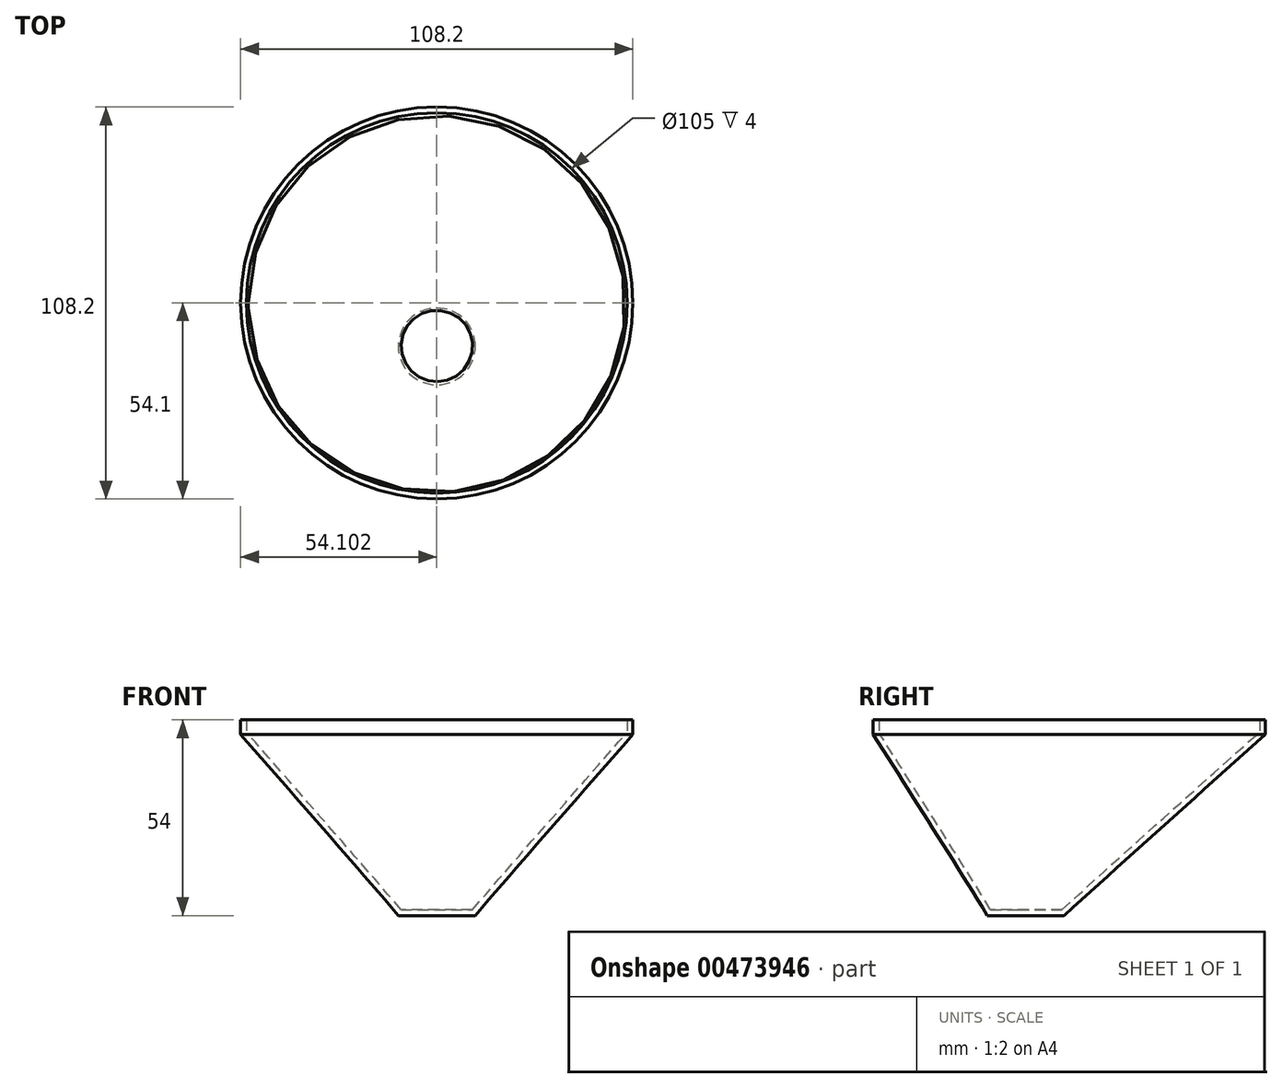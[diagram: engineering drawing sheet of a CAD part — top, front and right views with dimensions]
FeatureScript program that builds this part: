
annotation { "Feature Type Name" : "Feature", "Feature Type Description" : "" }
export const myFeature = defineFeature(function(context is Context, id is Id, definition is map)
    precondition{}
    {
        {
            var Q0;
            Q0=qCreatedBy(makeId("Top.planeOp"),FACE);
            var sketch = newSketch(context, id + "F0", { "sketchPlane" : qUnion([Q0])});
            skCircle(sketch, "E0", {"center": v(-6, 0) * mm, "radius": 52.5 * mm, "construction": true});
            skCircle(sketch, "E1.0", {"center": v(-6, 0) * mm, "radius": 54.1 * mm});
            skSolve(sketch);
        }
        {
            var Q0;
            Q0=qCreatedBy(makeId("Top.planeOp"),FACE);
            cPlane(context, id + "F1", {"entities" : qUnion([Q0]), "cplaneType" : CPlaneType.OFFSET, "offset" : 50 * mm, "oppositeDirection" : true, "width" : 150 * mm, "height" : 150 * mm});
        }
        {
            var Q0;
            Q0=qCreatedBy(id+"F1.planeOp",FACE);
            var sketch = newSketch(context, id + "F2", { "sketchPlane" : qUnion([Q0])});
            skPoint(sketch, "E2.0", {"position": v(-6, 0) * mm});
            skCircle(sketch, "E3", {"center": v(-6, -12) * mm, "radius": 9 * mm, "construction": true});
            skCircle(sketch, "E4.0", {"center": v(-6, -12) * mm, "radius": 10.6 * mm});
            skSolve(sketch);
        }
        {
            var Q0;
            Q0=makeQuery(id+"F0.imprint","IMPRINT",FACE,{"disambiguationData":[TD([[makeQuery(id+"F0.imprint","IMPRINT",EDGE,{"derivedFrom":sQuery(id+"F0.wireOp",EDGE,"E1.0")}),1.0]])]});
            var Q1;
            Q1=makeQuery(id+"F2.imprint","IMPRINT",FACE,{"disambiguationData":[TD([[makeQuery(id+"F2.imprint","IMPRINT",EDGE,{"derivedFrom":sQuery(id+"F2.wireOp",EDGE,"E4.0")}),1.0]])]});
            var Q2;
            Q2=sQuery(id+"F0.wireOp",EDGE,"E0");
            var Q3;
            Q3=sQuery(id+"F2.wireOp",EDGE,"E3");
            loft(context, id + "F3", {"sheetProfilesArray" : [{ "sheetProfileEntities" : qUnion([Q0]) }, { "sheetProfileEntities" : qUnion([Q1]) }], "wireProfilesArray" : [{ "wireProfileEntities" : qUnion([Q2]) }, { "wireProfileEntities" : qUnion([Q3]) }]});
        }
        {
            var Q0;
            Q0=makeQuery(id+"F3.opLoft","CAP_FACE",FACE,{"disambiguationData":[OSD([makeQuery(id+"F0.imprint","IMPRINT",FACE,{"disambiguationData":[TD([[makeQuery(id+"F0.imprint","IMPRINT",EDGE,{"derivedFrom":sQuery(id+"F0.wireOp",EDGE,"E1.0")}),1.0]])]})])],"isStart":true});
            shell(context, id + "F4", {"entities" : qUnion([Q0]), "thickness" : 1.6 * mm});
        }
        {
            var Q0;
            Q0=makeQuery(id+"F0.imprint","IMPRINT",FACE,{"disambiguationData":[TD([[makeQuery(id+"F0.imprint","IMPRINT",EDGE,{"derivedFrom":sQuery(id+"F0.wireOp",EDGE,"E1.0")}),1.0]])]});
            var sketch = newSketch(context, id + "F5", { "sketchPlane" : qUnion([Q0])});
            skCircle(sketch, "E5.0", {"center": v(-6, 0) * mm, "radius": 52.5 * mm});
            skCircle(sketch, "E6.0", {"center": v(-6, 0) * mm, "radius": 54.1 * mm});
            skSolve(sketch);
        }
        {
            var Q0;
            Q0=makeQuery(id+"F5.imprint","IMPRINT",FACE,{"disambiguationData":[TD([[makeQuery(id+"F5.imprint","IMPRINT",EDGE,{"derivedFrom":sQuery(id+"F5.wireOp",EDGE,"E5.0")}),-1.0]])]});
            extrude(context, id + "F6", {"entities" : qUnion([Q0]), "operationType" : NewBodyOperationType.ADD, "depth" : 4 * mm});
        }
    });
